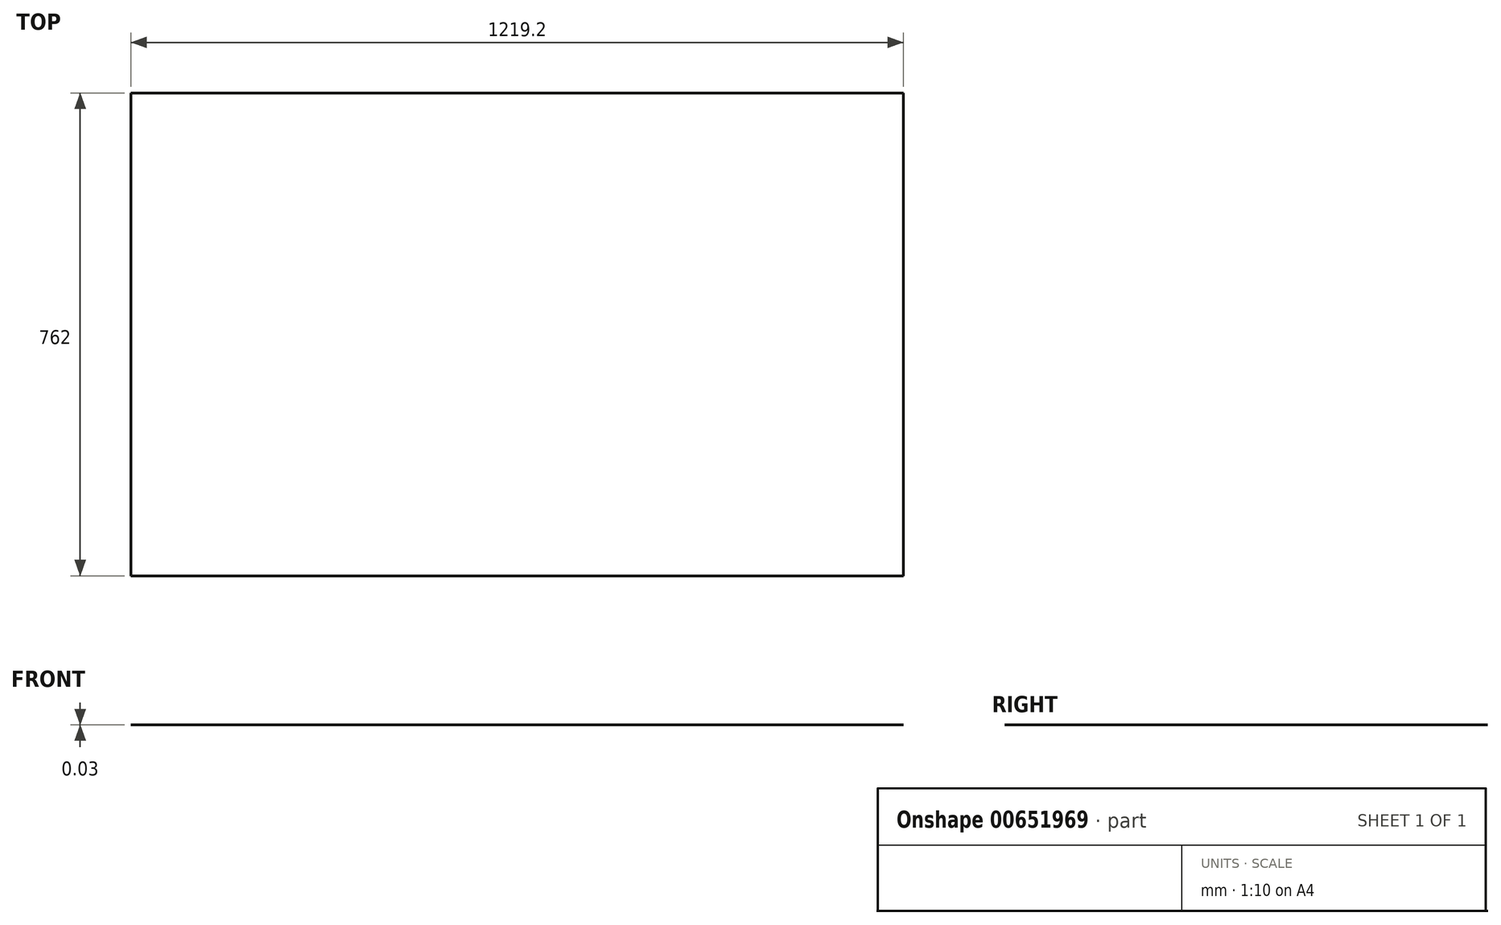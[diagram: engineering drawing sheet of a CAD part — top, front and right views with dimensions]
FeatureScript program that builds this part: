
annotation { "Feature Type Name" : "Feature", "Feature Type Description" : "" }
export const myFeature = defineFeature(function(context is Context, id is Id, definition is map)
    precondition{}
    {
        {
            var Q0;
            Q0=qCreatedBy(makeId("Top.planeOp"),FACE);
            var sketch = newSketch(context, id + "F0", { "sketchPlane" : qUnion([Q0])});
            skLineSegment(sketch, "E0.bottom", {"start": v(-680.52, 576.97) * mm, "end": v(538.68, 576.97) * mm});
            skLineSegment(sketch, "E0.top", {"start": v(-680.52, -185.03) * mm, "end": v(538.68, -185.03) * mm});
            skLineSegment(sketch, "E0.left", {"start": v(-680.52, 576.97) * mm, "end": v(-680.52, -185.03) * mm});
            skLineSegment(sketch, "E0.right", {"start": v(538.68, 576.97) * mm, "end": v(538.68, -185.03) * mm});
            skSolve(sketch);
        }
        {
            var Q0;
            Q0=makeQuery(id+"F0.imprint","IMPRINT",FACE,{"disambiguationData":[TD([[makeQuery(id+"F0.imprint","IMPRINT",EDGE,{"derivedFrom":sQuery(id+"F0.wireOp",EDGE,"E0.bottom")}),-1.0]])]});
            extrude(context, id + "F1", {"entities" : qUnion([Q0]), "depth" : 7 / 203.2 * mm, "offsetDistance" : 25.4 * mm});
        }
    });
